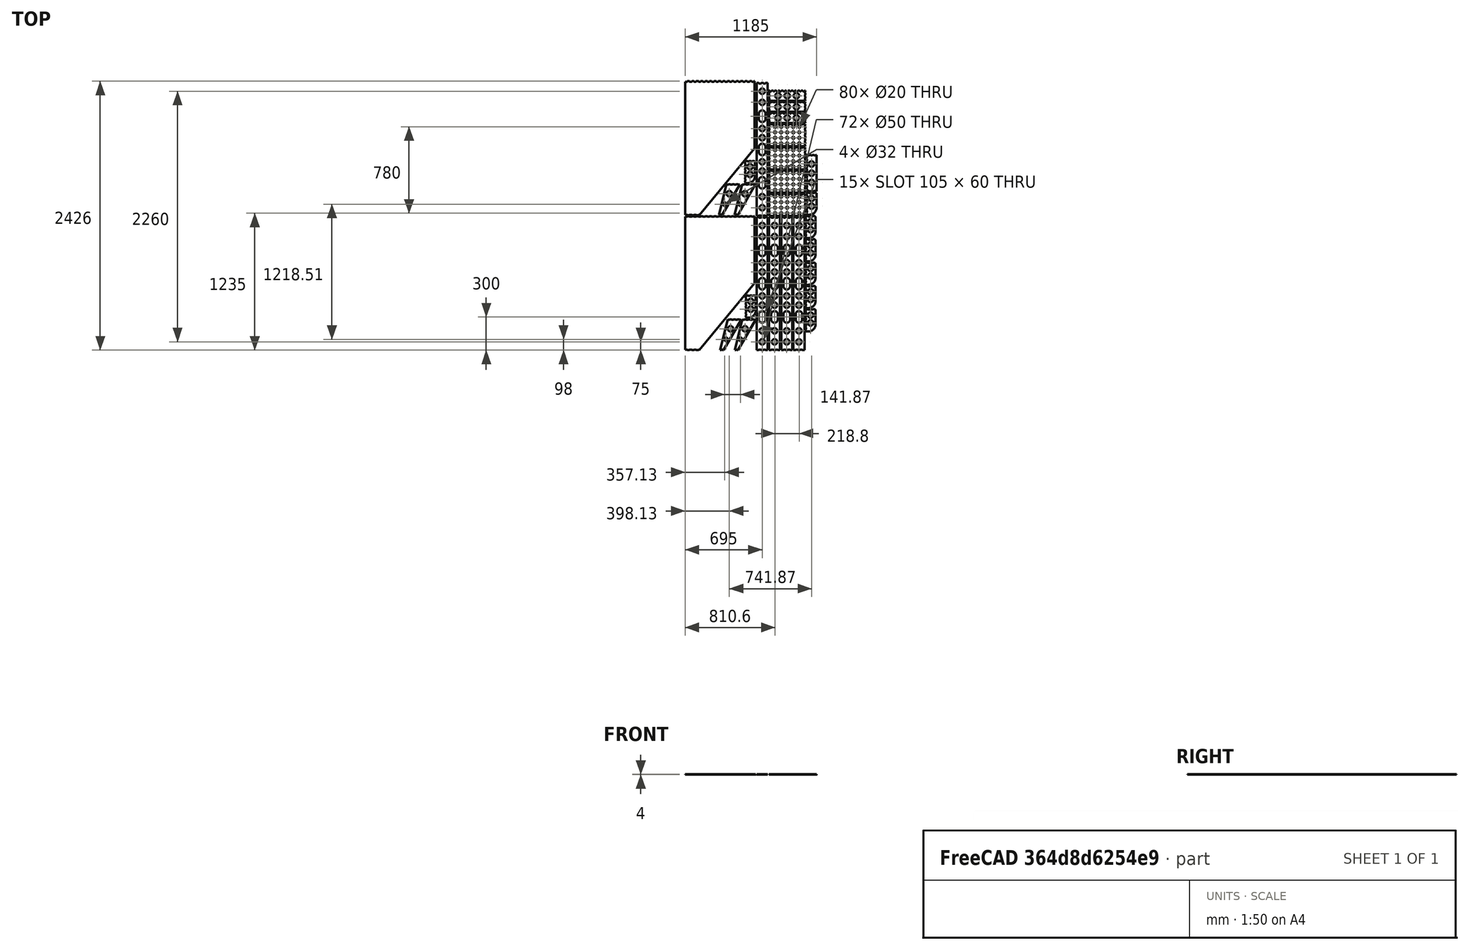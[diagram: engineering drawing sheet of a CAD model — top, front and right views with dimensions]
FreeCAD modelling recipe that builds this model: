
FCSTD DOCUMENT  (FreeCAD 0.19R24291 (Git))
Label: CAM-2
License: All rights reserved
LicenseURL: http://en.wikipedia.org/wiki/All_rights_reserved
objects: Part::Feature×27, Part::Part2DObjectPython×27
note: 54 computed .brp shape members not serialized (recipe doc carries the construction recipe); baked Part::Feature solids carry a one-line shape summary decoded from their .brp

FEATURE [Part::Feature] test
  Placement = pos=(52,604,1034) rot=(0,1,0;1.5708rad)
  shape: bbox 627 x 1208 x 4 mm, 82 faces (baked)
FEATURE [Part::Feature] test001
  Placement = pos=(52,1822,-970) rot=(0,1,0;1.5708rad)
  shape: bbox 627 x 1208 x 4 mm, 82 faces (baked)
FEATURE [Part::Feature] test002
  Placement = pos=(695,600,-634.66) rot=(0,1,0;1.5708rad)
  shape: bbox 100 x 1200 x 4 mm, 42 faces (baked)
FEATURE [Part::Feature] test003
  Placement = pos=(806,600,-301.33) rot=(0,1,0;1.5708rad)
  shape: bbox 100 x 1200 x 4 mm, 42 faces (baked)
FEATURE [Part::Feature] test004
  Placement = pos=(916,600,32) rot=(0,1,0;1.5708rad)
  shape: bbox 100 x 1200 x 4 mm, 42 faces (baked)
FEATURE [Part::Feature] test005
  Placement = pos=(695,1810,365.33) rot=(0,1,0;1.5708rad)
  shape: bbox 100 x 1200 x 4 mm, 42 faces (baked)
FEATURE [Part::Feature] test006
  Placement = pos=(1026,600,698.66) rot=(0,1,0;1.5708rad)
  shape: bbox 100 x 1200 x 4 mm, 42 faces (baked)
FEATURE [Part::Feature] test007
  Placement = pos=(425.13,2100.46,-570.4) rot=(0,1,0;1.5708rad)
  shape: bbox 187.7 x 277.1 x 4 mm, 25 faces (baked)
FEATURE [Part::Feature] test008
  Placement = pos=(567,882,-168.8) rot=(0,1,0;1.5708rad)
  shape: bbox 187.7 x 277.1 x 4 mm, 25 faces (baked)
FEATURE [Part::Feature] test009
  Placement = pos=(436,882,232.8) rot=(0,1,0;1.5708rad)
  shape: bbox 187.7 x 277.1 x 4 mm, 25 faces (baked)
FEATURE [Part::Feature] test010
  Placement = pos=(565.904,2100.51,634.4) rot=(0,1,0;1.5708rad)
  shape: bbox 187.7 x 277.1 x 4 mm, 25 faces (baked)
FEATURE [Part::Feature] test011
  Placement = pos=(1420,2295,336) rot=(1,0,0;1.5708rad)
  shape: bbox 328 x 90 x 4 mm, 77 faces (baked)
FEATURE [Part::Feature] test012
  Placement = pos=(420,1712,-11) rot=(0,1,0;3.14159rad)
  shape: bbox 328 x 200 x 4 mm, 126 faces (baked)
FEATURE [Part::Feature] test013
  Placement = pos=(1131,1512,-630) rot=(0,1,0;1.5708rad)
  shape: bbox 90 x 200 x 4 mm, 49 faces (baked)
FEATURE [Part::Feature] test014
  Placement = pos=(1131,1302,-306) rot=(0,1,0;1.5708rad)
  shape: bbox 90 x 200 x 4 mm, 49 faces (baked)
FEATURE [Part::Feature] test015
  Placement = pos=(1140,1763,336) rot=(0.57735,0.57735,0.57735;2.0944rad)
  shape: bbox 90 x 328 x 4 mm, 77 faces (baked)
FEATURE [Part::Feature] test016
  Placement = pos=(753,2132,-11) rot=(0,1,0;3.14159rad)
  shape: bbox 328 x 200 x 4 mm, 126 faces (baked)
FEATURE [Part::Feature] test017
  Placement = pos=(1131,882,-297) rot=(0,1,0;1.5708rad)
  shape: bbox 90 x 200 x 4 mm, 49 faces (baked)
FEATURE [Part::Feature] test018
  Placement = pos=(1131,1092,27) rot=(0,1,0;1.5708rad)
  shape: bbox 90 x 200 x 4 mm, 49 faces (baked)
FEATURE [Part::Feature] test019
  Placement = pos=(753,2095,336) rot=(1,0,0;1.5708rad)
  shape: bbox 328 x 90 x 4 mm, 77 faces (baked)
FEATURE [Part::Feature] test020
  Placement = pos=(1087,1922,-11) rot=(0,1,0;3.14159rad)
  shape: bbox 328 x 200 x 4 mm, 126 faces (baked)
FEATURE [Part::Feature] test021
  Placement = pos=(584.887,2009.3,37) rot=(0,1,0;1.5708rad)
  shape: bbox 90 x 200 x 4 mm, 49 faces (baked)
FEATURE [Part::Feature] test022
  Placement = pos=(1131,671,361) rot=(0,1,0;1.5708rad)
  shape: bbox 90 x 200 x 4 mm, 49 faces (baked)
FEATURE [Part::Feature] test023
  Placement = pos=(420,2195,336) rot=(1,0,0;1.5708rad)
  shape: bbox 328 x 90 x 4 mm, 77 faces (baked)
FEATURE [Part::Feature] test024
  Placement = pos=(1420,2342,-11) rot=(0,1,0;3.14159rad)
  shape: bbox 328 x 200 x 4 mm, 126 faces (baked)
FEATURE [Part::Feature] test025
  Placement = pos=(1140,1724,370) rot=(0,1,0;1.5708rad)
  shape: bbox 90 x 200 x 4 mm, 49 faces (baked)
FEATURE [Part::Feature] test026
  Placement = pos=(591.683,794.851,694) rot=(0,1,0;1.5708rad)
  shape: bbox 90 x 200 x 4 mm, 49 faces (baked)
FEATURE [Part::Part2DObjectPython] Shape2DView  # Draft 2D object (typed FeaturePython)
  Base = -> test
  FuseArch = false
  HiddenLines = false
  InPlace = true
  Projection = (0,0,1)
  ProjectionMode = 0
  SegmentLength = 0.05
  Tessellation = false
  VisibleOnly = false
FEATURE [Part::Part2DObjectPython] Shape2DView001  # Draft 2D object (typed FeaturePython)
  Base = -> test001
  FuseArch = false
  HiddenLines = false
  InPlace = true
  Projection = (0,0,1)
  ProjectionMode = 0
  SegmentLength = 0.05
  Tessellation = false
  VisibleOnly = false
FEATURE [Part::Part2DObjectPython] Shape2DView002  # Draft 2D object (typed FeaturePython)
  Base = -> test002
  FuseArch = false
  HiddenLines = false
  InPlace = true
  Projection = (0,0,1)
  ProjectionMode = 0
  SegmentLength = 0.05
  Tessellation = false
  VisibleOnly = false
FEATURE [Part::Part2DObjectPython] Shape2DView003  # Draft 2D object (typed FeaturePython)
  Base = -> test003
  FuseArch = false
  HiddenLines = false
  InPlace = true
  Projection = (0,0,1)
  ProjectionMode = 0
  SegmentLength = 0.05
  Tessellation = false
  VisibleOnly = false
FEATURE [Part::Part2DObjectPython] Shape2DView004  # Draft 2D object (typed FeaturePython)
  Base = -> test004
  FuseArch = false
  HiddenLines = false
  InPlace = true
  Projection = (0,0,1)
  ProjectionMode = 0
  SegmentLength = 0.05
  Tessellation = false
  VisibleOnly = false
FEATURE [Part::Part2DObjectPython] Shape2DView005  # Draft 2D object (typed FeaturePython)
  Base = -> test005
  FuseArch = false
  HiddenLines = false
  InPlace = true
  Projection = (0,0,1)
  ProjectionMode = 0
  SegmentLength = 0.05
  Tessellation = false
  VisibleOnly = false
FEATURE [Part::Part2DObjectPython] Shape2DView006  # Draft 2D object (typed FeaturePython)
  Base = -> test006
  FuseArch = false
  HiddenLines = false
  InPlace = true
  Projection = (0,0,1)
  ProjectionMode = 0
  SegmentLength = 0.05
  Tessellation = false
  VisibleOnly = false
FEATURE [Part::Part2DObjectPython] Shape2DView007  # Draft 2D object (typed FeaturePython)
  Base = -> test007
  FuseArch = false
  HiddenLines = false
  InPlace = true
  Projection = (0,0,1)
  ProjectionMode = 0
  SegmentLength = 0.05
  Tessellation = false
  VisibleOnly = false
FEATURE [Part::Part2DObjectPython] Shape2DView008  # Draft 2D object (typed FeaturePython)
  Base = -> test008
  FuseArch = false
  HiddenLines = false
  InPlace = true
  Projection = (0,0,1)
  ProjectionMode = 0
  SegmentLength = 0.05
  Tessellation = false
  VisibleOnly = false
FEATURE [Part::Part2DObjectPython] Shape2DView009  # Draft 2D object (typed FeaturePython)
  Base = -> test009
  FuseArch = false
  HiddenLines = false
  InPlace = true
  Projection = (0,0,1)
  ProjectionMode = 0
  SegmentLength = 0.05
  Tessellation = false
  VisibleOnly = false
FEATURE [Part::Part2DObjectPython] Shape2DView010  # Draft 2D object (typed FeaturePython)
  Base = -> test010
  FuseArch = false
  HiddenLines = false
  InPlace = true
  Projection = (0,0,1)
  ProjectionMode = 0
  SegmentLength = 0.05
  Tessellation = false
  VisibleOnly = false
FEATURE [Part::Part2DObjectPython] Shape2DView011  # Draft 2D object (typed FeaturePython)
  Base = -> test011
  FuseArch = false
  HiddenLines = false
  InPlace = true
  Projection = (0,0,1)
  ProjectionMode = 0
  SegmentLength = 0.05
  Tessellation = false
  VisibleOnly = false
FEATURE [Part::Part2DObjectPython] Shape2DView012  # Draft 2D object (typed FeaturePython)
  Base = -> test012
  FuseArch = false
  HiddenLines = false
  InPlace = true
  Projection = (0,0,1)
  ProjectionMode = 0
  SegmentLength = 0.05
  Tessellation = false
  VisibleOnly = false
FEATURE [Part::Part2DObjectPython] Shape2DView013  # Draft 2D object (typed FeaturePython)
  Base = -> test013
  FuseArch = false
  HiddenLines = false
  InPlace = true
  Projection = (0,0,1)
  ProjectionMode = 0
  SegmentLength = 0.05
  Tessellation = false
  VisibleOnly = false
FEATURE [Part::Part2DObjectPython] Shape2DView014  # Draft 2D object (typed FeaturePython)
  Base = -> test014
  FuseArch = false
  HiddenLines = false
  InPlace = true
  Projection = (0,0,1)
  ProjectionMode = 0
  SegmentLength = 0.05
  Tessellation = false
  VisibleOnly = false
FEATURE [Part::Part2DObjectPython] Shape2DView015  # Draft 2D object (typed FeaturePython)
  Base = -> test015
  FuseArch = false
  HiddenLines = false
  InPlace = true
  Projection = (0,0,1)
  ProjectionMode = 0
  SegmentLength = 0.05
  Tessellation = false
  VisibleOnly = false
FEATURE [Part::Part2DObjectPython] Shape2DView016  # Draft 2D object (typed FeaturePython)
  Base = -> test016
  FuseArch = false
  HiddenLines = false
  InPlace = true
  Projection = (0,0,1)
  ProjectionMode = 0
  SegmentLength = 0.05
  Tessellation = false
  VisibleOnly = false
FEATURE [Part::Part2DObjectPython] Shape2DView017  # Draft 2D object (typed FeaturePython)
  Base = -> test017
  FuseArch = false
  HiddenLines = false
  InPlace = true
  Projection = (0,0,1)
  ProjectionMode = 0
  SegmentLength = 0.05
  Tessellation = false
  VisibleOnly = false
FEATURE [Part::Part2DObjectPython] Shape2DView018  # Draft 2D object (typed FeaturePython)
  Base = -> test018
  FuseArch = false
  HiddenLines = false
  InPlace = true
  Projection = (0,0,1)
  ProjectionMode = 0
  SegmentLength = 0.05
  Tessellation = false
  VisibleOnly = false
FEATURE [Part::Part2DObjectPython] Shape2DView019  # Draft 2D object (typed FeaturePython)
  Base = -> test019
  FuseArch = false
  HiddenLines = false
  InPlace = true
  Projection = (0,0,1)
  ProjectionMode = 0
  SegmentLength = 0.05
  Tessellation = false
  VisibleOnly = false
FEATURE [Part::Part2DObjectPython] Shape2DView020  # Draft 2D object (typed FeaturePython)
  Base = -> test020
  FuseArch = false
  HiddenLines = false
  InPlace = true
  Projection = (0,0,1)
  ProjectionMode = 0
  SegmentLength = 0.05
  Tessellation = false
  VisibleOnly = false
FEATURE [Part::Part2DObjectPython] Shape2DView021  # Draft 2D object (typed FeaturePython)
  Base = -> test021
  FuseArch = false
  HiddenLines = false
  InPlace = true
  Projection = (0,0,1)
  ProjectionMode = 0
  SegmentLength = 0.05
  Tessellation = false
  VisibleOnly = false
FEATURE [Part::Part2DObjectPython] Shape2DView022  # Draft 2D object (typed FeaturePython)
  Base = -> test022
  FuseArch = false
  HiddenLines = false
  InPlace = true
  Projection = (0,0,1)
  ProjectionMode = 0
  SegmentLength = 0.05
  Tessellation = false
  VisibleOnly = false
FEATURE [Part::Part2DObjectPython] Shape2DView023  # Draft 2D object (typed FeaturePython)
  Base = -> test023
  FuseArch = false
  HiddenLines = false
  InPlace = true
  Projection = (0,0,1)
  ProjectionMode = 0
  SegmentLength = 0.05
  Tessellation = false
  VisibleOnly = false
FEATURE [Part::Part2DObjectPython] Shape2DView024  # Draft 2D object (typed FeaturePython)
  Base = -> test024
  FuseArch = false
  HiddenLines = false
  InPlace = true
  Projection = (0,0,1)
  ProjectionMode = 0
  SegmentLength = 0.05
  Tessellation = false
  VisibleOnly = false
FEATURE [Part::Part2DObjectPython] Shape2DView025  # Draft 2D object (typed FeaturePython)
  Base = -> test025
  FuseArch = false
  HiddenLines = false
  InPlace = true
  Projection = (0,0,1)
  ProjectionMode = 0
  SegmentLength = 0.05
  Tessellation = false
  VisibleOnly = false
FEATURE [Part::Part2DObjectPython] Shape2DView026  # Draft 2D object (typed FeaturePython)
  Base = -> test026
  FuseArch = false
  HiddenLines = false
  InPlace = true
  Projection = (0,0,1)
  ProjectionMode = 0
  SegmentLength = 0.05
  Tessellation = false
  VisibleOnly = false
